# Revit family: Faucet-Bath-KOHLER-Purist-K-T97328
name_source: partatom
category: Plumbing Fixtures
revit_build: Autodesk Revit 2015 (Build: 20140606_1530(x64)
units: mm (PartAtom-declared; Revit-internal decimal feet)

## types (5) — shared parameters
ADA = No
Assembly Code = D2020
CW Connection = Yes
Cold Water Inlet = Cold Water Inlet
Date Modified = 01/30/2018
Default Elevation = 36"
Description = Floor-mount bath filler trim with handshower
Faucet Hole Spacing = 0"
Flow Rate = 6 GPM
HW Connection = Yes
Height = 36 9/16"
Hot Water Inlet = Hot Water Inlet
Length = 15 1/32"
Manufacturer = KOHLER Co.
MasterFormat 1995 = 15410
MasterFormat 2004 = 22.41.39
Material = Premium Metal Construction
Pressure = 80.00 psi
Product Documentation Link = http://www.us.kohler.com
Product Name = Purist
Product Page URL = http://www.us.kohler.com
Spout Reach = 12 1/16"
URL = https://www.us.kohler.com
Vent Connection = No
Waste Connection = No
Waste Water Outlet = Waste Water Outlet
Width = 7 7/8"

## per-type parameters (varying)
| type | Finish | Model | Type |
| CP-Polished Chrome | Kohler-Metal-CP-Polished_Chrome | K-T97328-4-CP | 1 |
| SN-Vibrant Polished Nickel | Kohler-Metal-SN-Vibrant_Polished_Nickel | K-T97328-4-SN | 2 |
| BN-Vibrant Brushed Nickel | Kohler-Metal-BN-Vibrant_Brushed_Nickel | K-T97328-4-BN | 3 |
| BL-Matte Black | Kohler-Metal-BL-Matte_Black | K-T97328-4-BL | 4 |
| RGD-Polished Rose Gold | Kohler-Metal-RGD-Polished_Rose_Gold | K-T97328-4-RGD | 5 |

## geometry (parser evidence)
native form markers: Sweep x6
no freeform markers — native parametric forms only
